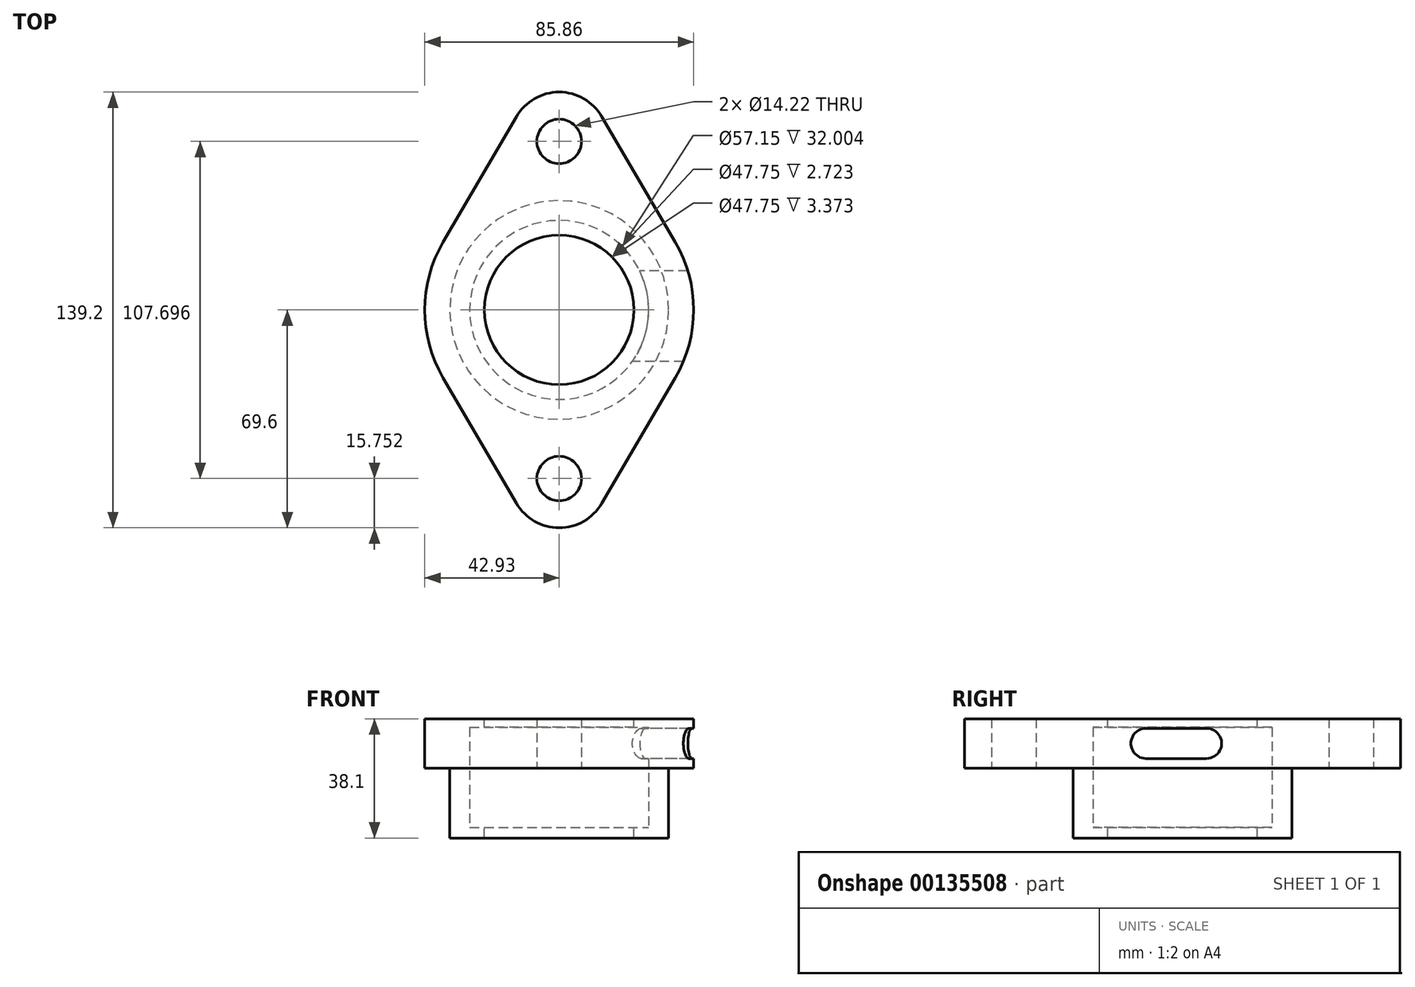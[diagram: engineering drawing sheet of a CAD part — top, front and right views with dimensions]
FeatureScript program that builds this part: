
annotation { "Feature Type Name" : "Feature", "Feature Type Description" : "" }
export const myFeature = defineFeature(function(context is Context, id is Id, definition is map)
    precondition{}
    {
        {
            var Q0;
            Q0=qCreatedBy(makeId("Top.planeOp"),FACE);
            var sketch = newSketch(context, id + "F0", { "sketchPlane" : qUnion([Q0])});
            skArc(sketch, "E0", {"start": v(10.06, -41.73) * mm, "mid": v(42.93, 0) * mm, "end": v(10.06, 41.73) * mm});
            skCircle(sketch, "E1", {"center": v(0, 53.85) * mm, "radius": 7.11 * mm});
            skCircle(sketch, "E2", {"center": v(0, -53.85) * mm, "radius": 7.11 * mm});
            skArc(sketch, "E3", {"start": v(10.06, 41.73) * mm, "mid": v(0, 69.6) * mm, "end": v(-10.06, 41.73) * mm});
            skArc(sketch, "E4", {"start": v(-10.06, -41.73) * mm, "mid": v(0, -69.6) * mm, "end": v(10.06, -41.73) * mm});
            skLineSegment(sketch, "E5", {"start": v(-13.6, 61.8) * mm, "end": v(-37.06, 21.67) * mm});
            skLineSegment(sketch, "E6", {"start": v(-13.6, -61.8) * mm, "end": v(-37.06, -21.67) * mm});
            skLineSegment(sketch, "E7", {"start": v(13.6, 61.8) * mm, "end": v(37.06, 21.67) * mm});
            skLineSegment(sketch, "E8", {"start": v(13.6, -61.8) * mm, "end": v(37.06, -21.67) * mm});
            skArc(sketch, "E9.trimOffspring", {"start": v(-10.06, 41.73) * mm, "mid": v(-42.93, 0) * mm, "end": v(-10.06, -41.73) * mm});
            skSolve(sketch);
        }
        {
            var Q0;
            Q0 = qSketchRegion(id + "F0", true);
            extrude(context, id + "F1", {"entities" : qUnion([Q0]), "depth" : 15.75 * mm});
        }
        {
            var Q0;
            Q0=makeQuery(id+"F1.opExtrude","CAP_FACE",FACE,{"disambiguationData":[OSD([sQuery(id+"F0.wireOp",EDGE,"E0"),sQuery(id+"F0.wireOp",EDGE,"E1"),sQuery(id+"F0.wireOp",EDGE,"E2"),sQuery(id+"F0.wireOp",EDGE,"E3"),sQuery(id+"F0.wireOp",EDGE,"E4"),sQuery(id+"F0.wireOp",EDGE,"E5"),sQuery(id+"F0.wireOp",EDGE,"E6"),sQuery(id+"F0.wireOp",EDGE,"E7"),sQuery(id+"F0.wireOp",EDGE,"E8"),sQuery(id+"F0.wireOp",EDGE,"E9.trimOffspring")])],"isStart":true});
            var sketch = newSketch(context, id + "F2", { "sketchPlane" : qUnion([Q0])});
            skCircle(sketch, "E10", {"center": v(0, 0) * mm, "radius": 34.92 * mm});
            skSolve(sketch);
        }
        {
            var Q0;
            Q0 = qSketchRegion(id + "F2", true);
            extrude(context, id + "F3", {"entities" : qUnion([Q0]), "operationType" : NewBodyOperationType.ADD, "depth" : 22.35 * mm});
        }
        {
            var Q0;
            Q0=makeQuery(id+"F1.opExtrude","CAP_FACE",FACE,{"disambiguationData":[OSD([sQuery(id+"F0.wireOp",EDGE,"E0"),sQuery(id+"F0.wireOp",EDGE,"E1"),sQuery(id+"F0.wireOp",EDGE,"E2"),sQuery(id+"F0.wireOp",EDGE,"E3"),sQuery(id+"F0.wireOp",EDGE,"E4"),sQuery(id+"F0.wireOp",EDGE,"E5"),sQuery(id+"F0.wireOp",EDGE,"E6"),sQuery(id+"F0.wireOp",EDGE,"E7"),sQuery(id+"F0.wireOp",EDGE,"E8"),sQuery(id+"F0.wireOp",EDGE,"E9.trimOffspring")])],"isStart":false});
            var sketch = newSketch(context, id + "F4", { "sketchPlane" : qUnion([Q0])});
            skCircle(sketch, "E11", {"center": v(0, 0) * mm, "radius": 23.88 * mm});
            skSolve(sketch);
        }
        {
            var Q0;
            Q0 = qSketchRegion(id + "F4", true);
            extrude(context, id + "F5", {"entities" : qUnion([Q0]), "operationType" : NewBodyOperationType.REMOVE, "endBound" : BoundingType.THROUGH_ALL, "oppositeDirection" : true, "depth" : 35.05 * mm});
        }
        {
            var Q0;
            Q0=qCreatedBy(makeId("Right.planeOp"),FACE);
            var sketch = newSketch(context, id + "F6", { "sketchPlane" : qUnion([Q0])});
            skPoint(sketch, "E12.middle", {"position": v(0, 0) * mm});
            skLineSegment(sketch, "E13", {"start": v(0, 13.02) * mm, "end": v(0, -18.98) * mm});
            skLineSegment(sketch, "E14", {"start": v(0, -18.98) * mm, "end": v(28.58, -18.98) * mm});
            skLineSegment(sketch, "E15", {"start": v(28.58, -18.98) * mm, "end": v(28.58, 13.02) * mm});
            skLineSegment(sketch, "E16", {"start": v(28.58, 13.02) * mm, "end": v(0, 13.02) * mm});
            skLineSegment(sketch, "E17", {"start": v(0, 43.7) * mm, "end": v(0, -32.18) * mm, "construction": true});
            skSolve(sketch);
        }
        {
            var Q0;
            Q0 = qSketchRegion(id + "F6", true);
            var Q1;
            Q1=sQuery(id+"F6.wireOp",EDGE,"E17");
            revolve(context, id + "F7", {"operationType" : NewBodyOperationType.REMOVE, "entities" : qUnion([Q0]), "axis" : qUnion([Q1]), "revolveType" : RevolveType.FULL, "oppositeDirection" : true});
        }
        {
            var Q0;
            Q0=qCreatedBy(makeId("Right.planeOp"),FACE);
            var sketch = newSketch(context, id + "F8", { "sketchPlane" : qUnion([Q0])});
            skCircle(sketch, "E18", {"center": v(7.68, 7.87) * mm, "radius": 4.83 * mm});
            skCircle(sketch, "E19", {"center": v(-11.63, 7.87) * mm, "radius": 4.83 * mm});
            skLineSegment(sketch, "E20", {"start": v(-11.63, 12.7) * mm, "end": v(7.68, 12.7) * mm});
            skLineSegment(sketch, "E21", {"start": v(-11.63, 3.05) * mm, "end": v(7.68, 3.05) * mm});
            skSolve(sketch);
        }
        {
            var Q0;
            Q0 = qSketchRegion(id + "F8", true);
            extrude(context, id + "F9", {"entities" : qUnion([Q0]), "operationType" : NewBodyOperationType.REMOVE, "endBound" : BoundingType.THROUGH_ALL, "depth" : 110.33 * mm});
        }
    });
